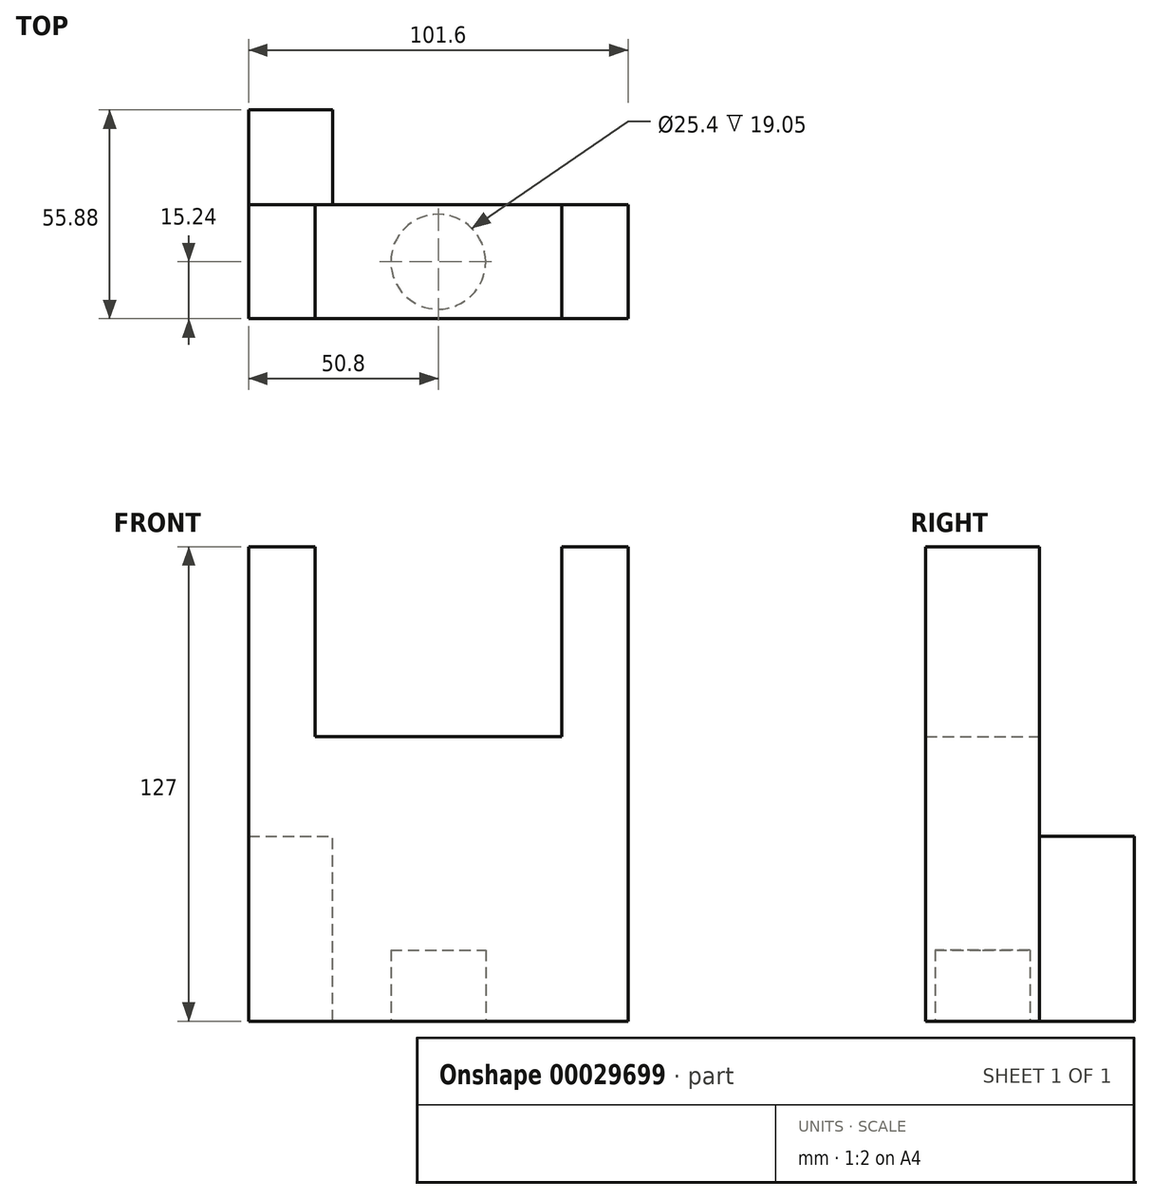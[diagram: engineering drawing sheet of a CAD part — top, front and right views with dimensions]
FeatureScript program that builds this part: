
annotation { "Feature Type Name" : "Feature", "Feature Type Description" : "" }
export const myFeature = defineFeature(function(context is Context, id is Id, definition is map)
    precondition{}
    {
        {
            var Q0;
            Q0=qCreatedBy(makeId("Front.planeOp"),FACE);
            var sketch = newSketch(context, id + "F0", { "sketchPlane" : qUnion([Q0])});
            skLineSegment(sketch, "E0.rect.bottom", {"start": v(50.8, -38.1) * mm, "end": v(-50.8, -38.1) * mm});
            skLineSegment(sketch, "E0.rect.top", {"start": v(50.8, 38.1) * mm, "end": v(-50.8, 38.1) * mm});
            skLineSegment(sketch, "E0.rect.left", {"start": v(50.8, -38.1) * mm, "end": v(50.8, 38.1) * mm});
            skLineSegment(sketch, "E0.rect.right", {"start": v(-50.8, -38.1) * mm, "end": v(-50.8, 38.1) * mm});
            skPoint(sketch, "E0.rect.middle", {"position": v(0, 0) * mm});
            skLineSegment(sketch, "E1.bottom", {"start": v(-50.8, 38.1) * mm, "end": v(-33.02, 38.1) * mm});
            skLineSegment(sketch, "E1.top", {"start": v(-50.8, 88.9) * mm, "end": v(-33.02, 88.9) * mm});
            skLineSegment(sketch, "E1.left", {"start": v(-50.8, 38.1) * mm, "end": v(-50.8, 88.9) * mm});
            skLineSegment(sketch, "E1.right", {"start": v(-33.02, 38.1) * mm, "end": v(-33.02, 88.9) * mm});
            skLineSegment(sketch, "E2.bottom", {"start": v(50.8, 38.1) * mm, "end": v(33.02, 38.1) * mm});
            skLineSegment(sketch, "E2.top", {"start": v(50.8, 88.9) * mm, "end": v(33.02, 88.9) * mm});
            skLineSegment(sketch, "E2.left", {"start": v(50.8, 38.1) * mm, "end": v(50.8, 88.9) * mm});
            skLineSegment(sketch, "E2.right", {"start": v(33.02, 38.1) * mm, "end": v(33.02, 88.9) * mm});
            skSolve(sketch);
        }
        {
            var Q0;
            Q0 = qSketchRegion(id + "F0", true);
            var Q1;
            Q1=makeQuery(id+"F0.imprint","IMPRINT",FACE,{"disambiguationData":[TD([[makeQuery(id+"F0.imprint","IMPRINT",EDGE,{"derivedFrom":sQuery(id+"F0.wireOp",EDGE,"E0.rect.bottom")}),-1.0]])]});
            extrude(context, id + "F1", {"entities" : qUnion([Q0, Q1]), "depth" : 30.48 * mm});
        }
        {
            var Q0;
            Q0=makeQuery(id+"F1.opExtrude","SWEPT_FACE",FACE,{"disambiguationData":[OSD([sQuery(id+"F0.wireOp",EDGE,"E0.rect.bottom")])]});
            var sketch = newSketch(context, id + "F2", { "sketchPlane" : qUnion([Q0])});
            skCircle(sketch, "E3", {"center": v(0, 15.24) * mm, "radius": 12.7 * mm});
            skSolve(sketch);
        }
        {
            var Q0;
            Q0 = qSketchRegion(id + "F2", true);
            var Q1;
            Q1=makeQuery(id+"F2.imprint","IMPRINT",FACE,{"disambiguationData":[TD([[makeQuery(id+"F2.imprint","IMPRINT",EDGE,{"derivedFrom":sQuery(id+"F2.wireOp",EDGE,"E3")}),1.0]])]});
            extrude(context, id + "F3", {"entities" : qUnion([Q0, Q1]), "operationType" : NewBodyOperationType.REMOVE, "oppositeDirection" : true, "depth" : 19.05 * mm});
        }
        {
            var Q0;
            Q0=makeQuery(id+"F1.opExtrude","CAP_FACE",FACE,{"disambiguationData":[OSD([sQuery(id+"F0.wireOp",EDGE,"E0.rect.bottom"),sQuery(id+"F0.wireOp",EDGE,"E0.rect.top"),sQuery(id+"F0.wireOp",EDGE,"E0.rect.left"),sQuery(id+"F0.wireOp",EDGE,"E0.rect.right"),sQuery(id+"F0.wireOp",EDGE,"E1.top"),sQuery(id+"F0.wireOp",EDGE,"E1.left"),sQuery(id+"F0.wireOp",EDGE,"E1.right"),sQuery(id+"F0.wireOp",EDGE,"E2.top"),sQuery(id+"F0.wireOp",EDGE,"E2.left"),sQuery(id+"F0.wireOp",EDGE,"E2.right")])],"isStart":true});
            var sketch = newSketch(context, id + "F4", { "sketchPlane" : qUnion([Q0])});
            skLineSegment(sketch, "E4.bottom", {"start": v(50.8, -38.1) * mm, "end": v(28.27, -38.1) * mm});
            skLineSegment(sketch, "E4.top", {"start": v(50.8, 11.37) * mm, "end": v(28.27, 11.37) * mm});
            skLineSegment(sketch, "E4.left", {"start": v(50.8, -38.1) * mm, "end": v(50.8, 11.37) * mm});
            skLineSegment(sketch, "E4.right", {"start": v(28.27, -38.1) * mm, "end": v(28.27, 11.37) * mm});
            skSolve(sketch);
        }
        {
            var Q0;
            Q0 = qSketchRegion(id + "F4", true);
            var Q1;
            Q1=makeQuery(id+"F4.imprint","IMPRINT",FACE,{"disambiguationData":[TD([[makeQuery(id+"F4.imprint","IMPRINT",EDGE,{"derivedFrom":sQuery(id+"F4.wireOp",EDGE,"E4.bottom")}),1.0]])]});
            extrude(context, id + "F5", {"entities" : qUnion([Q0, Q1]), "operationType" : NewBodyOperationType.ADD, "depth" : 25.4 * mm});
        }
    });
